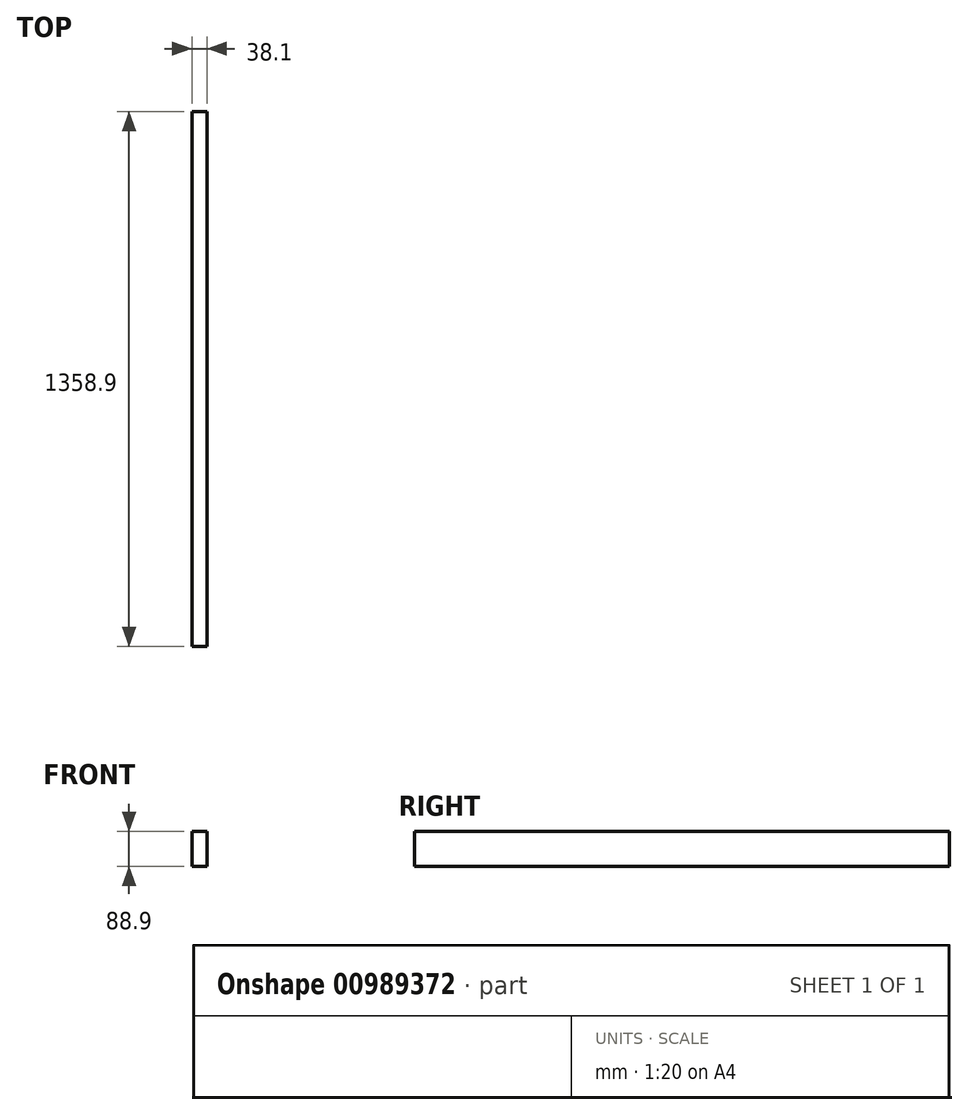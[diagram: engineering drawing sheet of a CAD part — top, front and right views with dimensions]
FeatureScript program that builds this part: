
annotation { "Feature Type Name" : "Feature", "Feature Type Description" : "" }
export const myFeature = defineFeature(function(context is Context, id is Id, definition is map)
    precondition{}
    {
        {
            var Q0;
            Q0=qCreatedBy(makeId("Front.planeOp"),FACE);
            var sketch = newSketch(context, id + "F0", { "sketchPlane" : qUnion([Q0])});
            skLineSegment(sketch, "E0.bottom", {"start": v(0, 0) * mm, "end": v(-38.1, 0) * mm});
            skLineSegment(sketch, "E0.top", {"start": v(0, 88.9) * mm, "end": v(-38.1, 88.9) * mm});
            skLineSegment(sketch, "E0.left", {"start": v(0, 0) * mm, "end": v(0, 88.9) * mm});
            skLineSegment(sketch, "E0.right", {"start": v(-38.1, 0) * mm, "end": v(-38.1, 88.9) * mm});
            skSolve(sketch);
        }
        {
            var Q0;
            Q0=makeQuery(id+"F0.imprint","IMPRINT",FACE,{"disambiguationData":[TD([[makeQuery(id+"F0.imprint","IMPRINT",EDGE,{"derivedFrom":sQuery(id+"F0.wireOp",EDGE,"E0.bottom")}),-1.0]])]});
            extrude(context, id + "F1", {"entities" : qUnion([Q0]), "depth" : 1358.9 * mm, "offsetDistance" : 25.4 * mm});
        }
    });
